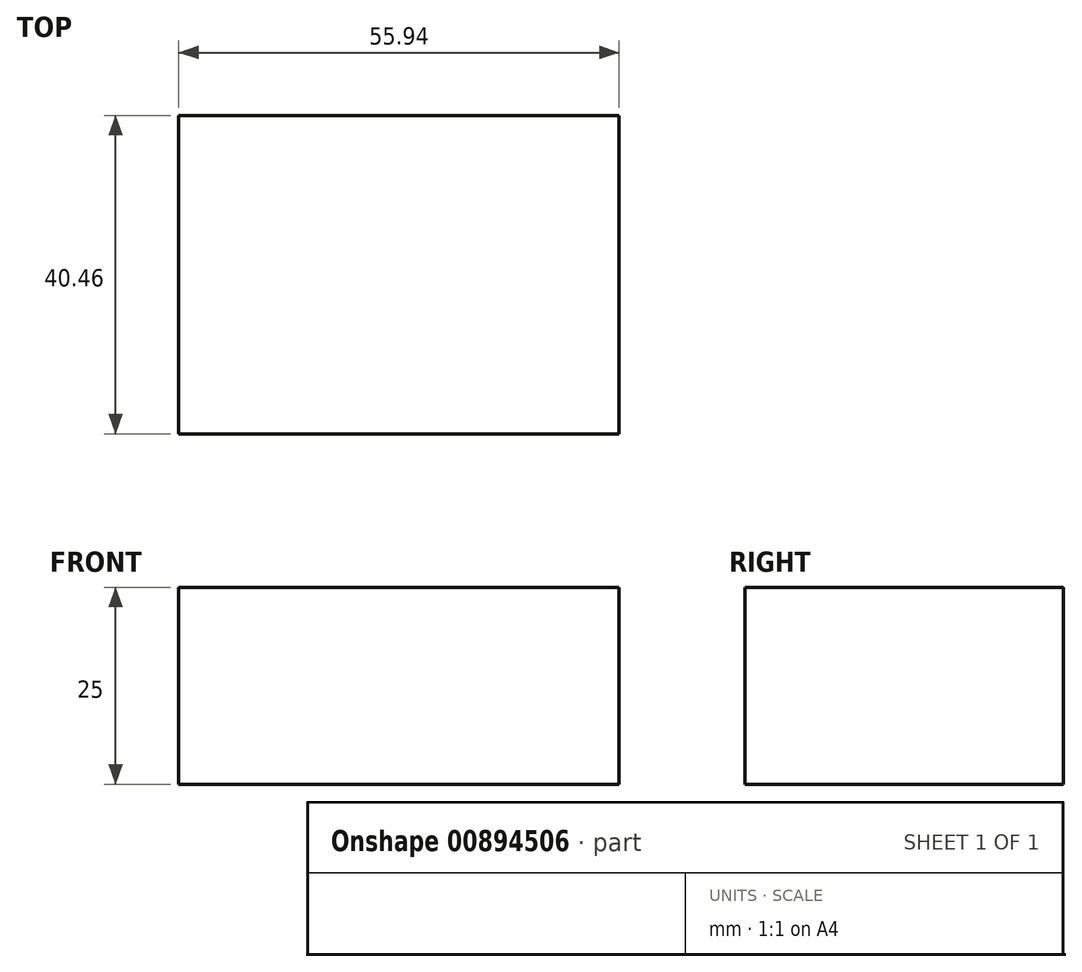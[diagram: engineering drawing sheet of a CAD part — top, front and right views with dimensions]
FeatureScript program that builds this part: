
annotation { "Feature Type Name" : "Feature", "Feature Type Description" : "" }
export const myFeature = defineFeature(function(context is Context, id is Id, definition is map)
    precondition{}
    {
        {
            var Q0;
            Q0=qCreatedBy(makeId("Top.planeOp"),FACE);
            var sketch = newSketch(context, id + "F0", { "sketchPlane" : qUnion([Q0])});
            skLineSegment(sketch, "E0.bottom", {"start": v(27.97, 20.23) * mm, "end": v(-27.97, 20.23) * mm});
            skLineSegment(sketch, "E0.top", {"start": v(27.97, -20.23) * mm, "end": v(-27.97, -20.23) * mm});
            skLineSegment(sketch, "E0.left", {"start": v(27.97, 20.23) * mm, "end": v(27.97, -20.23) * mm});
            skLineSegment(sketch, "E0.right", {"start": v(-27.97, 20.23) * mm, "end": v(-27.97, -20.23) * mm});
            skPoint(sketch, "E0.middle", {"position": v(0, 0) * mm});
            skSolve(sketch);
        }
        {
            var Q0;
            Q0 = qSketchRegion(id + "F0", true);
            extrude(context, id + "F1", {"entities" : qUnion([Q0]), "depth" : 25 * mm, "offsetDistance" : 25 * mm});
        }
    });
